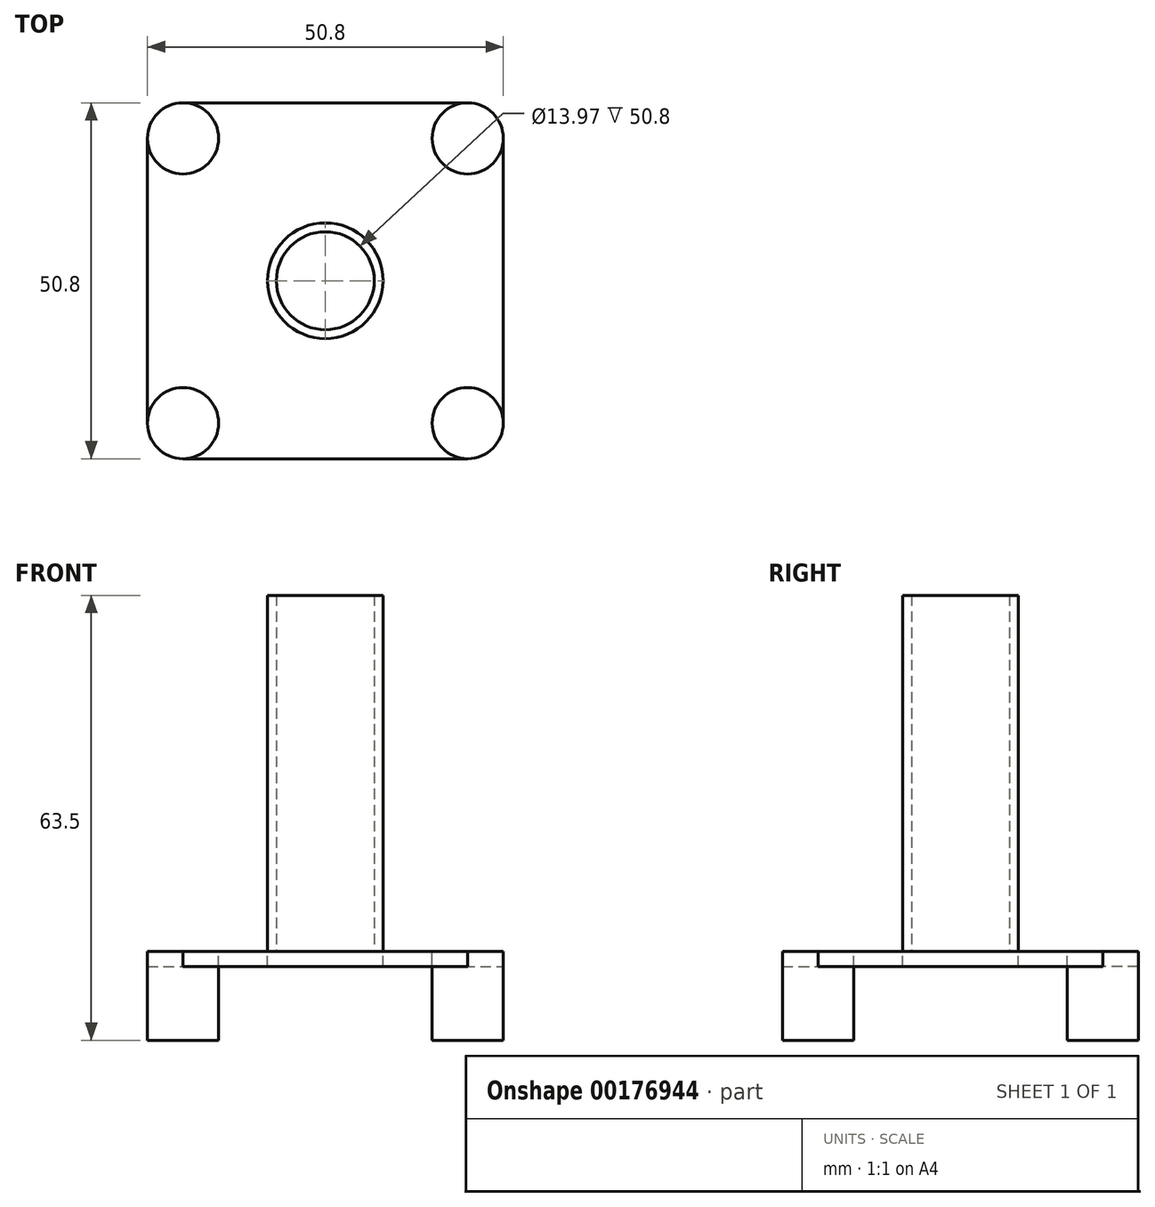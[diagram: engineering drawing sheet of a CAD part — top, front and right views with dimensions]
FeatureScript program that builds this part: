
annotation { "Feature Type Name" : "Feature", "Feature Type Description" : "" }
export const myFeature = defineFeature(function(context is Context, id is Id, definition is map)
    precondition{}
    {
        {
            var Q0;
            Q0=qCreatedBy(makeId("Top.planeOp"),FACE);
            var sketch = newSketch(context, id + "F0", { "sketchPlane" : qUnion([Q0])});
            skCircle(sketch, "E0", {"center": v(0, 0) * mm, "radius": 6.99 * mm});
            skCircle(sketch, "E1", {"center": v(0, 0) * mm, "radius": 8.26 * mm});
            skSolve(sketch);
        }
        {
            var Q0;
            Q0 = qSketchRegion(id + "F0", true);
            extrude(context, id + "F1", {"entities" : qUnion([Q0]), "depth" : 50.8 * mm});
        }
        {
            var Q0;
            Q0=makeQuery(id+"F1.opExtrude","CAP_FACE",FACE,{"disambiguationData":[OSD([sQuery(id+"F0.wireOp",EDGE,"E0"),sQuery(id+"F0.wireOp",EDGE,"E1")])],"isStart":true});
            var sketch = newSketch(context, id + "F2", { "sketchPlane" : qUnion([Q0])});
            skLineSegment(sketch, "E2.bottom", {"start": v(20.32, -25.4) * mm, "end": v(-20.32, -25.4) * mm});
            skLineSegment(sketch, "E2.top", {"start": v(20.32, 25.4) * mm, "end": v(-20.32, 25.4) * mm});
            skLineSegment(sketch, "E2.left", {"start": v(25.4, -20.32) * mm, "end": v(25.4, 20.32) * mm});
            skLineSegment(sketch, "E2.right", {"start": v(-25.4, -20.32) * mm, "end": v(-25.4, 20.32) * mm});
            skPoint(sketch, "E2.middle", {"position": v(0, 0) * mm});
            skPoint(sketch, "E3.visualSharp", {"position": v(25.4, 25.4) * mm});
            skArc(sketch, "E3.filletArc", {"start": v(25.4, 20.32) * mm, "mid": v(23.91, 23.91) * mm, "end": v(20.32, 25.4) * mm});
            skPoint(sketch, "E4.visualSharp", {"position": v(25.4, -25.4) * mm});
            skArc(sketch, "E4.filletArc", {"start": v(20.32, -25.4) * mm, "mid": v(23.91, -23.91) * mm, "end": v(25.4, -20.32) * mm});
            skPoint(sketch, "E5.visualSharp", {"position": v(-25.4, -25.4) * mm});
            skArc(sketch, "E5.filletArc", {"start": v(-25.4, -20.32) * mm, "mid": v(-23.91, -23.91) * mm, "end": v(-20.32, -25.4) * mm});
            skPoint(sketch, "E6.visualSharp", {"position": v(-25.4, 25.4) * mm});
            skArc(sketch, "E6.filletArc", {"start": v(-20.32, 25.4) * mm, "mid": v(-23.91, 23.91) * mm, "end": v(-25.4, 20.32) * mm});
            skCircle(sketch, "E7", {"center": v(-20.32, 20.32) * mm, "radius": 5.08 * mm});
            skCircle(sketch, "E8", {"center": v(20.32, 20.32) * mm, "radius": 5.08 * mm});
            skCircle(sketch, "E9", {"center": v(20.32, -20.32) * mm, "radius": 5.08 * mm});
            skCircle(sketch, "E10", {"center": v(-20.32, -20.32) * mm, "radius": 5.08 * mm});
            skSolve(sketch);
        }
        {
            var Q0;
            {var subQ0=sQuery(id+"F2.wireOp",EDGE,"E7");var subQ1=makeQuery(id+"F2.imprint","INTERSECT",VERTEX,{"derivedFrom":[sQuery(id+"F2.wireOp",EDGE,"E2.top"),subQ0]});Q0=makeQuery(id+"F2.imprint","IMPRINT",FACE,{"disambiguationData":[TD([[makeQuery(id+"F2.imprint","IMPRINT",EDGE,{"disambiguationData":[TD([[subQ1,-1.0]])],"derivedFrom":subQ0}),1.0]])]});}
            var Q1;
            {var subQ0=sQuery(id+"F2.wireOp",EDGE,"E8");var subQ1=makeQuery(id+"F2.imprint","INTERSECT",VERTEX,{"derivedFrom":[sQuery(id+"F2.wireOp",EDGE,"E2.top"),subQ0]});Q1=makeQuery(id+"F2.imprint","IMPRINT",FACE,{"disambiguationData":[TD([[makeQuery(id+"F2.imprint","IMPRINT",EDGE,{"disambiguationData":[TD([[subQ1,1.0]])],"derivedFrom":subQ0}),1.0]])]});}
            var Q2;
            {var subQ0=sQuery(id+"F2.wireOp",EDGE,"E9");var subQ1=makeQuery(id+"F2.imprint","INTERSECT",VERTEX,{"derivedFrom":[sQuery(id+"F2.wireOp",EDGE,"E2.bottom"),subQ0]});Q2=makeQuery(id+"F2.imprint","IMPRINT",FACE,{"disambiguationData":[TD([[makeQuery(id+"F2.imprint","IMPRINT",EDGE,{"disambiguationData":[TD([[subQ1,1.0]])],"derivedFrom":subQ0}),1.0]])]});}
            var Q3;
            {var subQ0=sQuery(id+"F2.wireOp",EDGE,"E10");var subQ1=makeQuery(id+"F2.imprint","INTERSECT",VERTEX,{"derivedFrom":[sQuery(id+"F2.wireOp",EDGE,"E2.bottom"),subQ0]});Q3=makeQuery(id+"F2.imprint","IMPRINT",FACE,{"disambiguationData":[TD([[makeQuery(id+"F2.imprint","IMPRINT",EDGE,{"disambiguationData":[TD([[subQ1,1.0]])],"derivedFrom":subQ0}),1.0]])]});}
            extrude(context, id + "F3", {"entities" : qUnion([Q0, Q1, Q2, Q3]), "depth" : 12.7 * mm});
        }
        {
            var Q0;
            {var subQ3=sQuery(id+"F2.wireOp",EDGE,"E2.bottom");Q0=makeQuery(id+"F2.imprint","IMPRINT",FACE,{"disambiguationData":[TD([[makeQuery(id+"F2.imprint","IMPRINT",EDGE,{"derivedFrom":subQ3}),-1.0]])]});}
            extrude(context, id + "F4", {"entities" : qUnion([Q0]), "depth" : 2.16 * mm});
        }
    });
